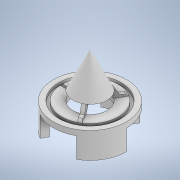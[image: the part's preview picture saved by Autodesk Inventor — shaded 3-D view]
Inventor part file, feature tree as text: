
AUTODESK INVENTOR PART (.ipt)
format: ipt  version: 2022.4 (Build 264492010, 492A)  size: 235,008 bytes
history: native  units: mm
features: sketch x7, extrude x5, revolve x1, plane x1, pattern_circular x1
ambient origin geometry x8: Origin, YZ Plane, XZ Plane, XY Plane, X Axis, Y Axis, Z Axis, Center Point
bodies: Solid1 (feature_tree)
feature tree (15):
  revolve  "Revolution1"  [1 undecoded]
  plane  "Work Plane1"
  extrude  "Extrusion1"  [1 undecoded]
  extrude  "Extrusion2"  Depth=82.5mm
  pattern_circular  "Circular Pattern1"  Count=3 Angle=360.0deg
  sketch  "Sketch5"  dims[d9=8.0mm d10=0.0mm]
  extrude  "Extrusion3"  Depth=57.0mm
  extrude  "Extrusion4"  Depth=25.0mm
  extrude  "Extrusion5"  Depth=30.0mm
  sketch  "Sketch1"  dims[d1=60.0mm d2=13.0mm]
  sketch  "Sketch3"  dims[d3=90.0deg d6=-5.0mm]
  sketch  "Sketch4"  dims[d7=50.0mm d8=82.5mm]
  sketch  "Sketch6"  dims[d11=5.0mm d12=0.0mm d13=30.0mm d14=360.0deg]
  sketch  "Sketch7"  dims[d16=79.0mm d17=57.0mm]
  sketch  "Sketch8"  dims[d18=5.0mm d19=25.0mm d20=82.5mm d21=4.5mm d22=8.0mm d23=0.0mm d24=4.0mm d25=0.0mm d26=0.0mm d27=10.0mm d28=120.0deg d29=120.0deg d30=120.0deg d31=30.0mm d32=0.0mm]
note: 2 required parameter values undecoded (feature->parameter linkage not recoverable at this tier; creation-order binding heuristic only, values carry confidence <= 0.55)